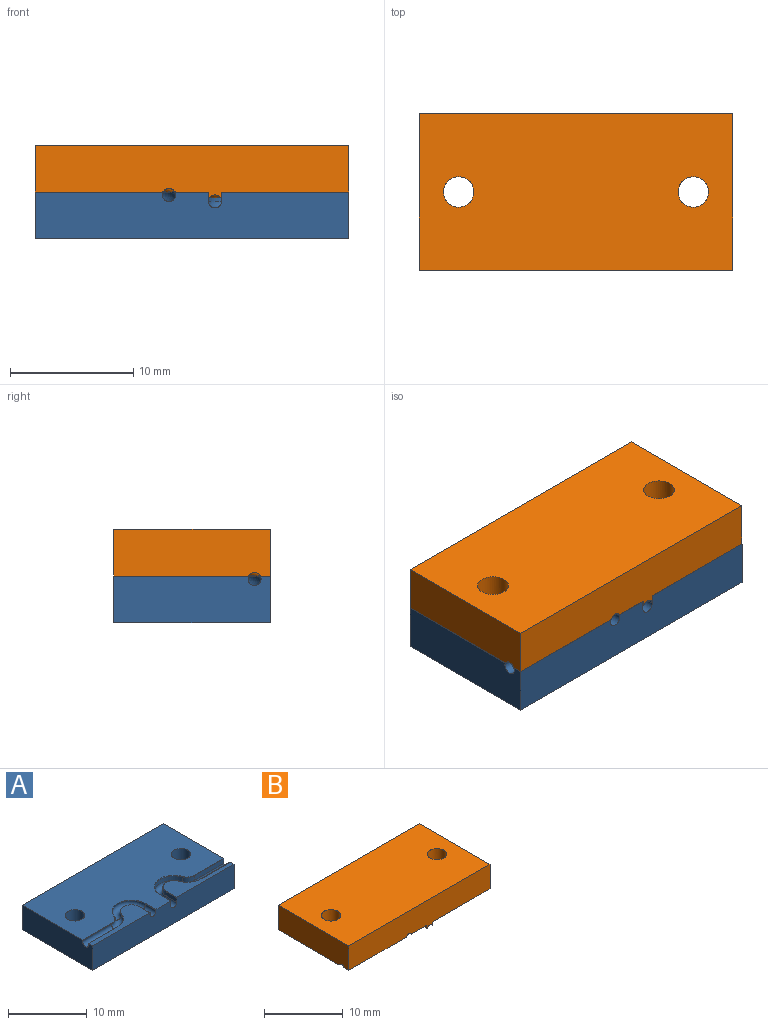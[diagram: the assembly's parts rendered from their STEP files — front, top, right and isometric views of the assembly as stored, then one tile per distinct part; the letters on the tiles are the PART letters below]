
ASSEMBLY  parts=2 mates=1
PART A: 42 faces, bbox 25.4x12.7x3.9 mm
  f0: plane 25.4x3.81mm, normal (0,-1,0), area 94.8mm2, adj f1,f2,f3,f4,f6,f7,f17,f18
  f1: plane 10.3x3.31mm, normal (0,0,1), area 14.9mm2, adj f0,f2,f38,f39,f40,f41
  f2: plane 12.7x3.81mm, normal (-1,0,0), area 47.7mm2, adj f0,f1,f3,f5,f6,f22,f26,f39
  f3: plane 25.4x12.7mm, normal (0,0,1), area 250.5mm2, adj f0,f2,f4,f5,f20,f21,f26,f27
  f4: plane 12.7x3.81mm, normal (1,0,0), area 47.1mm2, adj f0,f3,f5,f6,f7,f8,f9,f10
  f5: plane 25.4x3.81mm, normal (0,1,0), area 96.8mm2, adj f2,f3,f4,f6
  f6: plane 25.4x12.7mm, normal (0,0,-1), area 312.8mm2, adj f0,f2,f4,f5,f20,f21
  f7: plane 10.26x3.28mm, normal (0,0,1), area 14.4mm2, adj f0,f4,f34,f35,f36,f37
  f8: plane 5.23x0.72mm, normal (0,-1,0), area 3.8mm2, adj f4,f9,f11,f30
  f9: cylinder r=0.53mm len=5.23mm, axis (-1,0,0), area 8.8mm2, adj f4,f8,f10,f12
  f10: plane 5.23x0.72mm, normal (0,1,0), area 3.8mm2, adj f4,f9,f13,f34
  f11: cylinder r=1.41mm len=1.33mm, axis (0,0,-1), area 1.3mm2, adj f8,f12,f14,f31
  f12: torus R=1.94mm, axis (0,0,-1), area 4mm2, adj f9,f11,f13,f15
  f13: cylinder r=2.48mm len=2.33mm, axis (0,0,-1), area 2.2mm2, adj f10,f12,f16,f35
  f14: cylinder r=2.48mm len=4.81mm, axis (0,0,1), area 5mm2, adj f11,f15,f17,f32
  f15: torus R=1.94mm, axis (0,0,1), area 9.1mm2, adj f12,f14,f16,f18
  f16: cylinder r=1.41mm len=2.74mm, axis (0,0,1), area 2.9mm2, adj f13,f15,f19,f36
  f17: plane 1.91x0.72mm, normal (1,0,0), area 1.4mm2, adj f0,f14,f18,f33
  f18: cylinder r=0.53mm len=1.91mm, axis (0,-1,0), area 3.2mm2, adj f0,f15,f17,f19
  f19: plane 1.91x0.72mm, normal (-1,0,0), area 1.4mm2, adj f0,f16,f18,f37
  f20: cylinder r=1.24mm len=3.81mm, axis (0,0,1), area 29.8mm2, adj f3,f6
  f21: cylinder r=1.24mm len=3.81mm, axis (0,0,1), area 29.8mm2, adj f3,f6
  f22: cylinder r=0.53mm len=5.23mm, axis (1,0,0), area 10.8mm2, adj f2,f23,f26,f39
  f23: torus R=1.94mm, axis (0,0,1), area 4.9mm2, adj f22,f24,f27,f41
  f24: torus R=1.94mm, axis (0,0,-1), area 11.2mm2, adj f23,f25,f28,f40
  f25: cylinder r=0.53mm len=1.91mm, axis (0,-1,0), area 3.9mm2, adj f0,f24,f29,f38
  f26: cylinder r=0.04mm len=5.23mm, axis (1,0,0), area 0.4mm2, adj f2,f3,f22,f27
  f27: torus R=1.41mm, axis (0,0,-1), area 0.1mm2, adj f3,f23,f26,f28
  f28: torus R=2.48mm, axis (0,0,1), area 0.5mm2, adj f3,f24,f27,f29
  f29: cylinder r=0.04mm len=1.91mm, axis (0,-1,0), area 0.1mm2, adj f0,f3,f25,f28
  f30: cylinder r=0.04mm len=5.23mm, axis (1,0,0), area 0.3mm2, adj f3,f4,f8,f31
  f31: torus R=1.37mm, axis (0,0,1), area 0.1mm2, adj f3,f11,f30,f32
  f32: torus R=2.51mm, axis (0,0,1), area 0.4mm2, adj f3,f14,f31,f33
  f33: cylinder r=0.04mm len=1.91mm, axis (0,1,0), area 0.1mm2, adj f0,f3,f17,f32
  f34: cylinder r=0.04mm len=5.23mm, axis (1,0,0), area 0.3mm2, adj f4,f7,f10,f35
  f35: torus R=2.51mm, axis (0,0,1), area 0.2mm2, adj f7,f13,f34,f36
  f36: torus R=1.37mm, axis (0,0,1), area 0.2mm2, adj f7,f16,f35,f37
  f37: cylinder r=0.04mm len=1.91mm, axis (0,1,0), area 0.1mm2, adj f0,f7,f19,f36
  f38: cylinder r=0.04mm len=1.91mm, axis (0,-1,0), area 0.1mm2, adj f0,f1,f25,f40
  f39: cylinder r=0.04mm len=5.23mm, axis (1,0,0), area 0.4mm2, adj f1,f2,f22,f41
  f40: torus R=1.41mm, axis (0,0,-1), area 0.3mm2, adj f1,f24,f38,f41
  f41: torus R=2.48mm, axis (0,0,1), area 0.2mm2, adj f1,f23,f39,f40
PART B: 42 faces, bbox 25.4x12.7x4.6 mm
  f0: plane 25.4x4.29mm, normal (0,-1,0), area 96.9mm2, adj f1,f5,f6,f7,f9,f10,f11,f15
  f1: plane 12.7x4.29mm, normal (1,0,0), area 48.7mm2, adj f0,f2,f7,f8,f10,f11,f16,f23
  f2: cylinder r=0.53mm len=5.23mm, axis (-1,0,0), area 5.4mm2, adj f1,f3,f27,f31
  f3: torus R=1.94mm, axis (0,0,-1), area 2.5mm2, adj f2,f4,f26,f30
  f4: torus R=1.94mm, axis (0,0,1), area 5.6mm2, adj f3,f5,f25,f29
  f5: cylinder r=0.53mm len=1.91mm, axis (0,-1,0), area 2mm2, adj f0,f4,f24,f28
  f6: plane 10.33x3.35mm, normal (0,0,-1), area 15.4mm2, adj f0,f9,f32,f33,f34,f35
  f7: plane 10.33x3.34mm, normal (0,0,-1), area 15.3mm2, adj f0,f1,f16,f17,f18,f19
  f8: plane 25.4x3.81mm, normal (0,1,0), area 96.8mm2, adj f1,f9,f10,f11
  f9: plane 12.7x3.81mm, normal (-1,0,0), area 48.2mm2, adj f0,f6,f8,f10,f11,f12,f35,f39
  f10: plane 25.4x12.7mm, normal (0,0,1), area 312.8mm2, adj f0,f1,f8,f9,f40,f41
  f11: plane 25.4x12.7mm, normal (0,0,-1), area 252mm2, adj f0,f1,f8,f9,f20,f21,f22,f23
  f12: cylinder r=0.53mm len=5.23mm, axis (1,0,0), area 5.9mm2, adj f9,f13,f35,f39
  f13: torus R=1.94mm, axis (0,0,1), area 2.7mm2, adj f12,f14,f34,f38
  f14: torus R=1.94mm, axis (0,0,-1), area 6.1mm2, adj f13,f15,f33,f37
  f15: cylinder r=0.53mm len=1.91mm, axis (0,-1,0), area 2.2mm2, adj f0,f14,f32,f36
  f16: plane 5.23x0.44mm, normal (0,-1,0), area 2.3mm2, adj f1,f7,f17,f31
  f17: cylinder r=2.45mm len=2.31mm, axis (0,0,-1), area 1.3mm2, adj f7,f16,f18,f30
  f18: cylinder r=1.44mm len=2.79mm, axis (0,0,1), area 1.8mm2, adj f7,f17,f19,f29
  f19: plane 1.91x0.44mm, normal (1,0,0), area 0.8mm2, adj f0,f7,f18,f28
  f20: plane 1.91x0.44mm, normal (-1,0,0), area 0.8mm2, adj f0,f11,f21,f24
  f21: cylinder r=2.45mm len=4.76mm, axis (0,0,1), area 3mm2, adj f11,f20,f22,f25
  f22: cylinder r=1.44mm len=1.35mm, axis (0,0,-1), area 0.8mm2, adj f11,f21,f23,f26
  f23: plane 5.23x0.44mm, normal (0,1,0), area 2.3mm2, adj f1,f11,f22,f27
  f24: cylinder r=0.04mm len=1.91mm, axis (0,-1,0), area 0.2mm2, adj f0,f5,f20,f25
  f25: torus R=2.41mm, axis (0,0,1), area 0.7mm2, adj f4,f21,f24,f26
  f26: torus R=1.47mm, axis (0,0,-1), area 0.2mm2, adj f3,f22,f25,f27
  f27: cylinder r=0.04mm len=5.23mm, axis (-1,0,0), area 0.5mm2, adj f1,f2,f23,f26
  f28: cylinder r=0.04mm len=1.91mm, axis (0,-1,0), area 0.2mm2, adj f0,f5,f19,f29
  f29: torus R=1.47mm, axis (0,0,-1), area 0.4mm2, adj f4,f18,f28,f30
  f30: torus R=2.41mm, axis (0,0,1), area 0.3mm2, adj f3,f17,f29,f31
  f31: cylinder r=0.04mm len=5.23mm, axis (-1,0,0), area 0.5mm2, adj f1,f2,f16,f30
  f32: cylinder r=0.04mm len=1.91mm, axis (0,-1,0), area 0.1mm2, adj f0,f6,f15,f33
  f33: torus R=1.44mm, axis (0,0,-1), area 0.2mm2, adj f6,f14,f32,f34
  f34: torus R=2.44mm, axis (0,0,1), area 0.1mm2, adj f6,f13,f33,f35
  f35: cylinder r=0.04mm len=5.23mm, axis (1,0,0), area 0.2mm2, adj f6,f9,f12,f34
  f36: cylinder r=0.04mm len=1.91mm, axis (0,-1,0), area 0.1mm2, adj f0,f11,f15,f37
  f37: torus R=2.44mm, axis (0,0,1), area 0.3mm2, adj f11,f14,f36,f38
  f38: torus R=1.44mm, axis (0,0,-1), area 0.1mm2, adj f11,f13,f37,f39
  f39: cylinder r=0.04mm len=5.23mm, axis (1,0,0), area 0.2mm2, adj f9,f11,f12,f38
  f40: cylinder r=1.24mm len=3.81mm, axis (0,0,-1), area 29.8mm2, adj f10,f11
  f41: cylinder r=1.24mm len=3.81mm, axis (0,0,-1), area 29.8mm2, adj f10,f11
PLACE A t=(0.1,2.59,3.65)mm
PLACE B t=(0,0,3.65)mm
MATE planar B.f11 <-> A.f3  axis (0,0,-1) through (12.8,3.47,3.65)mm
